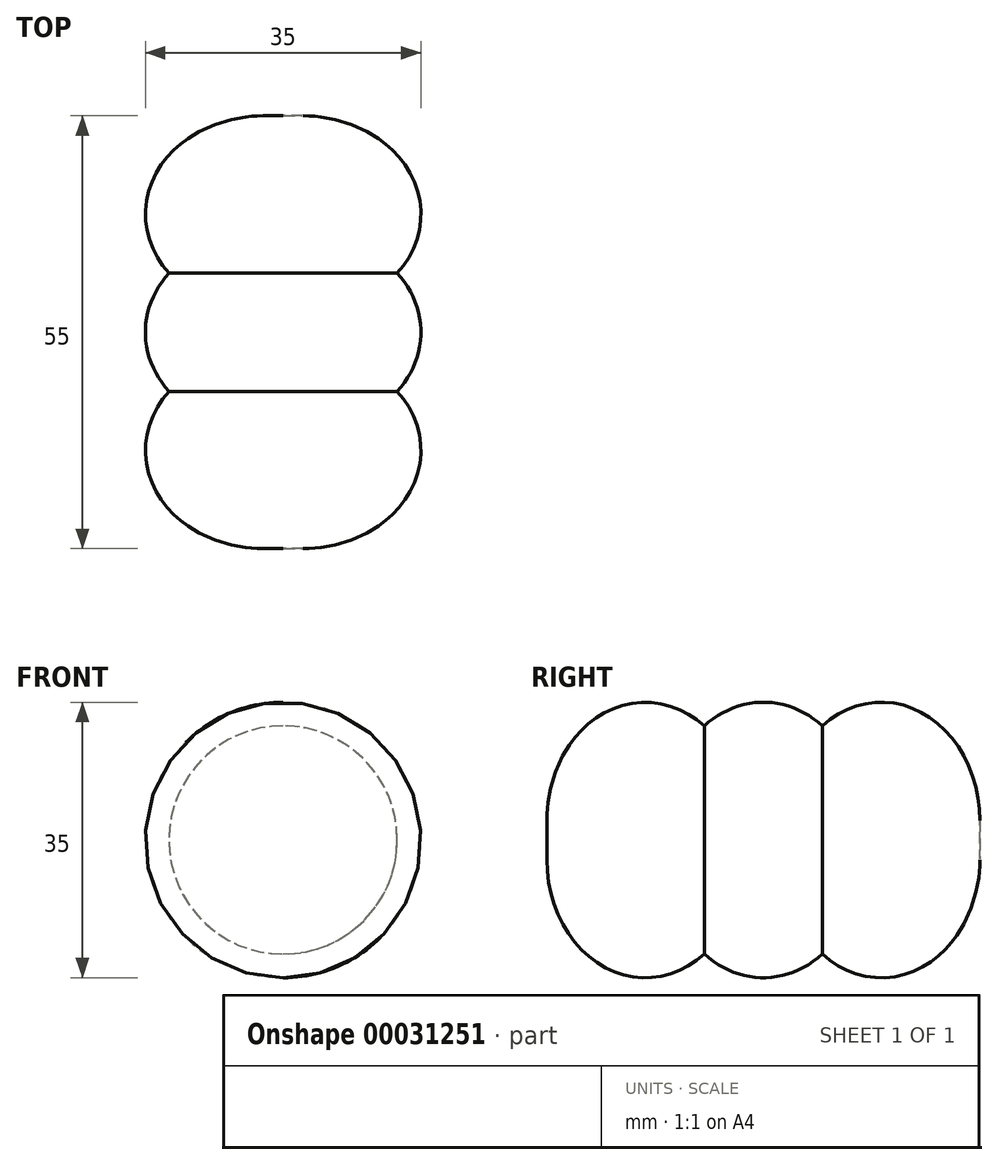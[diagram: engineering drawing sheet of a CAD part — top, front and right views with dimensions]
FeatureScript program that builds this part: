
annotation { "Feature Type Name" : "Feature", "Feature Type Description" : "" }
export const myFeature = defineFeature(function(context is Context, id is Id, definition is map)
    precondition{}
    {
        {
            var Q0;
            Q0=qCreatedBy(makeId("Top.planeOp"),FACE);
            var sketch = newSketch(context, id + "F0", { "sketchPlane" : qUnion([Q0])});
            skEllipticalArc(sketch, "E0", {});
            skPoint(sketch, "E1", {"position": v(0, 12.5) * mm});
            skPoint(sketch, "E2", {"position": v(15, 0) * mm});
            skLineSegment(sketch, "E3", {"start": v(0, 12.5) * mm, "end": v(0, -12.5) * mm, "construction": true});
            skLineSegment(sketch, "E4", {"start": v(0, 12.5) * mm, "end": v(-2.5, 12.5) * mm});
            skLineSegment(sketch, "E5", {"start": v(-2.5, 12.5) * mm, "end": v(-2.5, -12.5) * mm});
            skLineSegment(sketch, "E6", {"start": v(-2.5, -12.5) * mm, "end": v(0, -12.5) * mm});
            const initialGuessF0  = {"E0": [0, 0, 0, 1, 0.0125, 0.015, 3.141592653589793, 6.283185307179586]};
            skSetInitialGuess(sketch, initialGuessF0);
            skSolve(sketch);
        }
        {
            var Q0;
            Q0=makeQuery(id+"F0.imprint","IMPRINT",FACE,{"disambiguationData":[TD([[makeQuery(id+"F0.imprint","IMPRINT",EDGE,{"derivedFrom":sQuery(id+"F0.wireOp",EDGE,"E0")}),1.0]])]});
            var Q1;
            Q1=sQuery(id+"F0.wireOp",EDGE,"E5");
            revolve(context, id + "F1", {"entities" : qUnion([Q0]), "axis" : qUnion([Q1]), "revolveType" : RevolveType.FULL});
        }
        {
            var Q0;
            Q0=qCreatedBy(makeId("Front.planeOp"),FACE);
            cPlane(context, id + "F2", {"entities" : qUnion([Q0]), "cplaneType" : CPlaneType.OFFSET, "offset" : 7.5 * mm, "oppositeDirection" : true, "width" : 150 * mm, "height" : 150 * mm});
        }
        {
            var Q0;
            Q0=makeQuery(id+"F1.opRevolve","SWEPT_BODY",BODY,{"disambiguationData":[OSD([sQuery(id+"F0.wireOp",EDGE,"E0"),sQuery(id+"F0.wireOp",EDGE,"E4"),sQuery(id+"F0.wireOp",EDGE,"E5"),sQuery(id+"F0.wireOp",EDGE,"E6")])]});
            var Q1;
            Q1=qCreatedBy(id+"F2.planeOp",FACE);
            mirror(context, id + "F3", {"operationType" : NewBodyOperationType.ADD, "entities" : qUnion([Q0]), "mirrorPlane" : qUnion([Q1])});
        }
        {
            var Q0;
            Q0=makeQuery(id+"F1.opRevolve","SWEPT_BODY",BODY,{"disambiguationData":[OSD([sQuery(id+"F0.wireOp",EDGE,"E0"),sQuery(id+"F0.wireOp",EDGE,"E4"),sQuery(id+"F0.wireOp",EDGE,"E5"),sQuery(id+"F0.wireOp",EDGE,"E6")])]});
            var Q1;
            Q1=qCreatedBy(makeId("Front.planeOp"),FACE);
            mirror(context, id + "F4", {"operationType" : NewBodyOperationType.ADD, "entities" : qUnion([Q0]), "mirrorPlane" : qUnion([Q1])});
        }
    });
